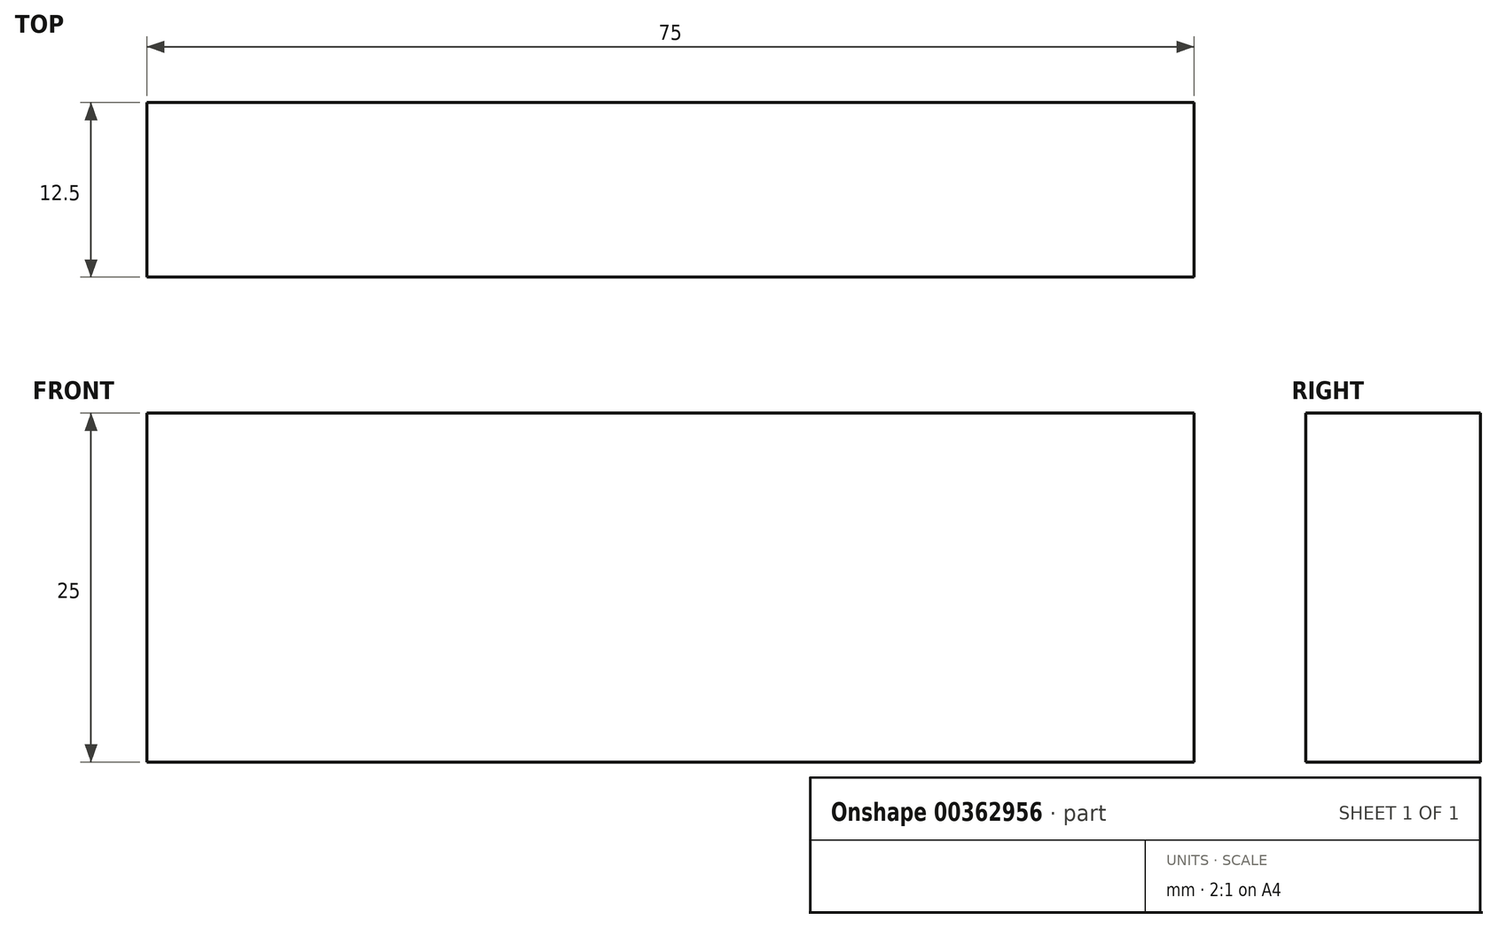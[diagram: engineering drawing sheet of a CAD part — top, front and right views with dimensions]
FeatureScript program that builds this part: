
annotation { "Feature Type Name" : "Feature", "Feature Type Description" : "" }
export const myFeature = defineFeature(function(context is Context, id is Id, definition is map)
    precondition{}
    {
        {
            var Q0;
            Q0=qCreatedBy(makeId("Front.planeOp"),FACE);
            var sketch = newSketch(context, id + "F0", { "sketchPlane" : qUnion([Q0])});
            skLineSegment(sketch, "E0.bottom", {"start": v(27.12, 33.62) * mm, "end": v(-47.88, 33.62) * mm});
            skLineSegment(sketch, "E0.top", {"start": v(27.12, 8.62) * mm, "end": v(-47.88, 8.62) * mm});
            skLineSegment(sketch, "E0.left", {"start": v(27.12, 33.62) * mm, "end": v(27.12, 8.62) * mm});
            skLineSegment(sketch, "E0.right", {"start": v(-47.88, 33.62) * mm, "end": v(-47.88, 8.62) * mm});
            skSolve(sketch);
        }
        {
            var Q0;
            Q0=makeQuery(id+"F0.imprint","IMPRINT",FACE,{"disambiguationData":[TD([[makeQuery(id+"F0.imprint","IMPRINT",EDGE,{"derivedFrom":sQuery(id+"F0.wireOp",EDGE,"E0.bottom")}),1.0]])]});
            extrude(context, id + "F1", {"entities" : qUnion([Q0]), "depth" : 12.5 * mm});
        }
    });
